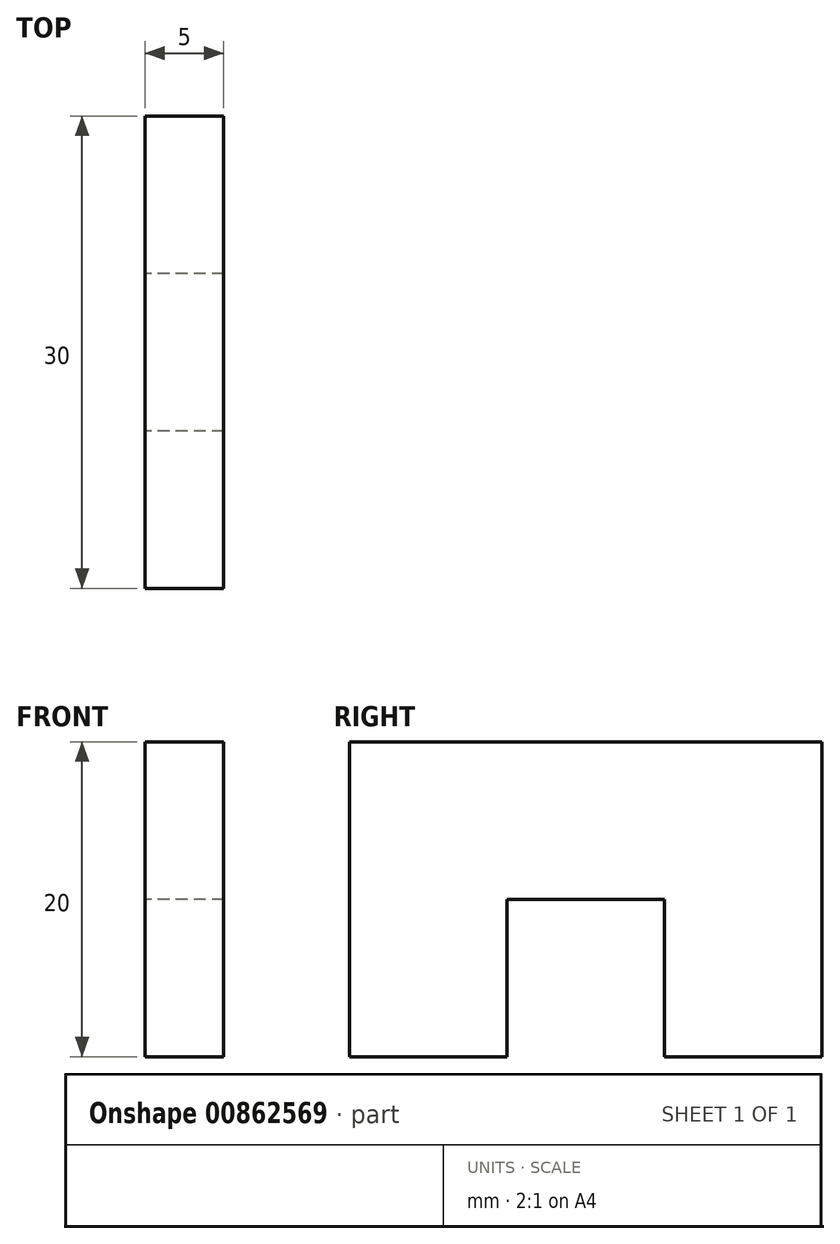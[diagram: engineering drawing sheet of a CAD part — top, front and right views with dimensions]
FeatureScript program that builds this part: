
annotation { "Feature Type Name" : "Feature", "Feature Type Description" : "" }
export const myFeature = defineFeature(function(context is Context, id is Id, definition is map)
    precondition{}
    {
        {
            var Q0;
            Q0=qCreatedBy(makeId("Right.planeOp"),FACE);
            var sketch = newSketch(context, id + "F0", { "sketchPlane" : qUnion([Q0])});
            skLineSegment(sketch, "E0.bottom", {"start": v(15, -10) * mm, "end": v(5, -10) * mm});
            skLineSegment(sketch, "E0.top", {"start": v(15, 10) * mm, "end": v(-15, 10) * mm});
            skLineSegment(sketch, "E0.left", {"start": v(15, -10) * mm, "end": v(15, 10) * mm});
            skLineSegment(sketch, "E0.right", {"start": v(-15, -10) * mm, "end": v(-15, 10) * mm});
            skPoint(sketch, "E0.middle", {"position": v(0, 0) * mm});
            skLineSegment(sketch, "E1", {"start": v(0, 0) * mm, "end": v(-5, 0) * mm});
            skLineSegment(sketch, "E2", {"start": v(-5, 0) * mm, "end": v(-5, -10) * mm});
            skLineSegment(sketch, "E3.MirrorCS", {"start": v(5, 0) * mm, "end": v(5, -10) * mm});
            skLineSegment(sketch, "E4.MirrorCS", {"start": v(0, 0) * mm, "end": v(5, 0) * mm});
            skLineSegment(sketch, "E5.trimOffspring", {"start": v(-5, -10) * mm, "end": v(-15, -10) * mm});
            skSolve(sketch);
        }
        {
            var Q0;
            Q0=makeQuery(id+"F0.imprint","IMPRINT",FACE,{"disambiguationData":[TD([[makeQuery(id+"F0.imprint","IMPRINT",EDGE,{"derivedFrom":sQuery(id+"F0.wireOp",EDGE,"E0.bottom")}),-1.0]])]});
            extrude(context, id + "F1", {"entities" : qUnion([Q0]), "depth" : 5 * mm, "offsetDistance" : 25 * mm});
        }
    });
